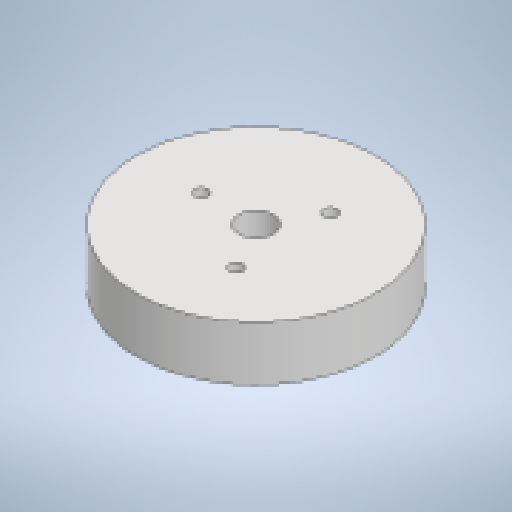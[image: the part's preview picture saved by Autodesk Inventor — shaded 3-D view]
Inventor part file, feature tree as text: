
AUTODESK INVENTOR PART (.ipt)
format: ipt  version: 2023.2 (Build 272271000, 271)  size: 429,568 bytes
history: native  units: in
note: dims shown in document units (in); Inventor stores cm internally (conversion verified against a paired STEP export)
features: thicken_offset x5, other x4, extrude x2, sketch x2, surface_op x1, plane x1
ambient origin geometry x8: Origin, YZ Plane, XZ Plane, XY Plane, X Axis, Y Axis, Z Axis, Center Point
bodies: Solid1 (feature_tree)
feature tree (15):
  extrude  "Extrusion1"  Depth=1.378in
  surface_op  "Sculpt1"
  plane  "Work Plane1"
  extrude  "Extrusion2"  Depth=0.0787in
  thicken_offset  "Thicken1"
  thicken_offset  "Thicken2"
  thicken_offset  "Thicken3"
  thicken_offset  "Thicken4"
  thicken_offset  "Thicken5"
  sketch  "Sketch1"  dims[d0=0.1969in d1=1.378in]
  sketch  "Sketch2"  dims[d2=0.6299in d3=0.0787in d4=1.1811in d6=360.0deg d8=0.315in d9=0.0in d10=0.0625in d11=0.6299in d12=1.378in d13=1.1811in d15=360.0deg d17=1.1811in d19=360.0deg d21=0.1575in d22=0.0in d23=2.3622in d25=360.0deg d27=0.0039in d28=0.0039in d29=0.0039in d30=0.0039in d31=0.0039in d32=0.0039in d33=0.0039in d34=0.0039in d35=0.0039in d36=0.0039in]
  other  "Composite1"
  other  "Srf1"
  other  "Flash Hobby D3530 1100KV.iam"
  other  "Body - Basic:1"
